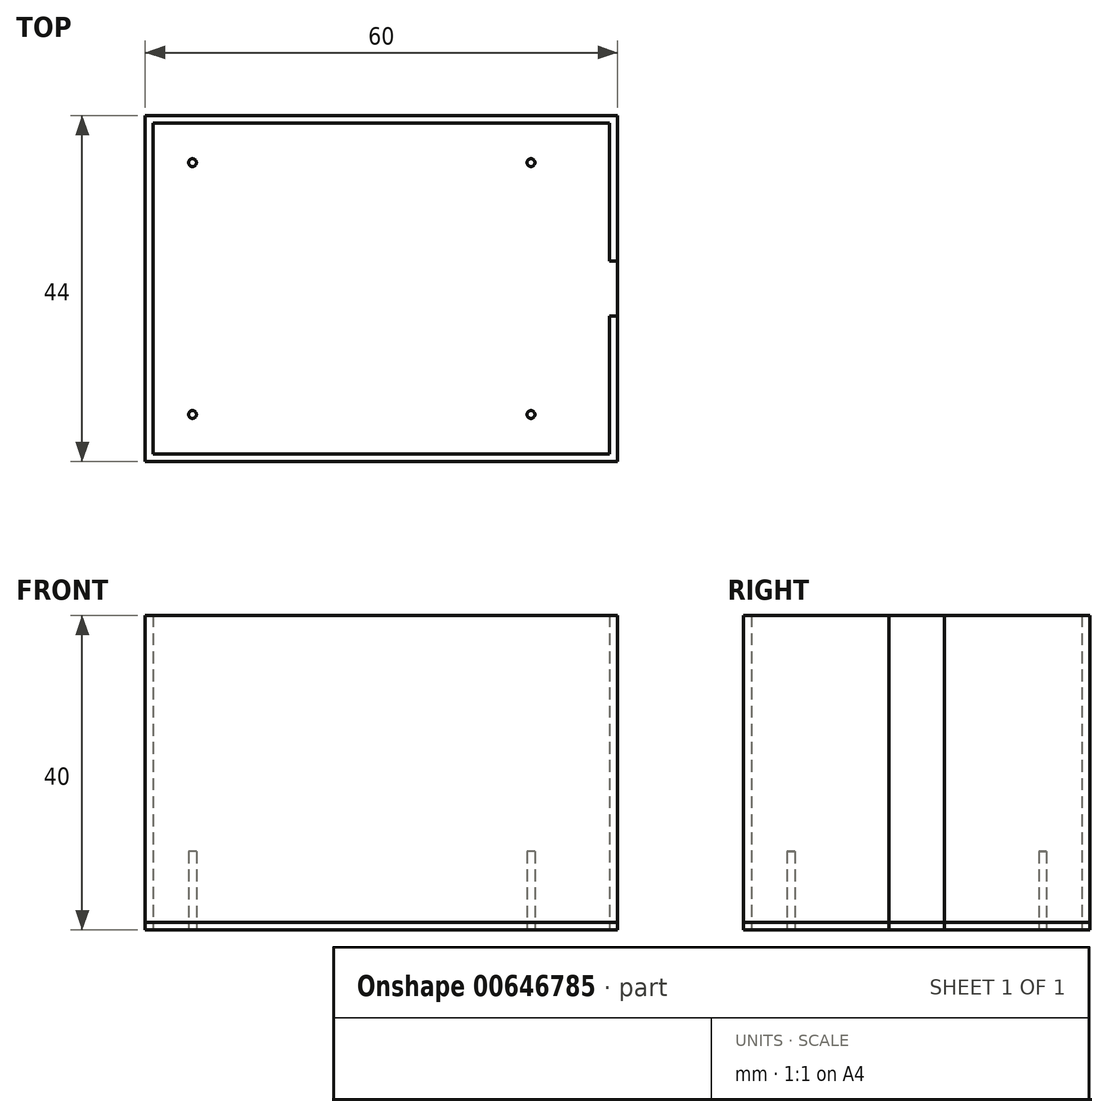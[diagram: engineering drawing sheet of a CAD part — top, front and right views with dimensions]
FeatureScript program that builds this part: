
annotation { "Feature Type Name" : "Feature", "Feature Type Description" : "" }
export const myFeature = defineFeature(function(context is Context, id is Id, definition is map)
    precondition{}
    {
        {
            var Q0;
            Q0=qCreatedBy(makeId("Top.planeOp"),FACE);
            var sketch = newSketch(context, id + "F0", { "sketchPlane" : qUnion([Q0])});
            skLineSegment(sketch, "E0", {"start": v(-43, 0) * mm, "end": v(0, 0) * mm});
            skLineSegment(sketch, "E1", {"start": v(0, 0) * mm, "end": v(0, 32) * mm});
            skLineSegment(sketch, "E2", {"start": v(0, 32) * mm, "end": v(-43, 32) * mm});
            skLineSegment(sketch, "E3", {"start": v(-43, 32) * mm, "end": v(-43, 0) * mm});
            skLineSegment(sketch, "E4.0", {"start": v(-48, -5) * mm, "end": v(10, -5) * mm});
            skLineSegment(sketch, "E4.1", {"start": v(-48, 37) * mm, "end": v(-48, -5) * mm});
            skLineSegment(sketch, "E4.2", {"start": v(10, 37) * mm, "end": v(-48, 37) * mm});
            skLineSegment(sketch, "E5.0", {"start": v(10, -5) * mm, "end": v(10, 37) * mm});
            skCircle(sketch, "E6", {"center": v(-43, 32) * mm, "radius": 0.5 * mm});
            skCircle(sketch, "E7", {"center": v(0, 32) * mm, "radius": 0.5 * mm});
            skCircle(sketch, "E8", {"center": v(-43, 0) * mm, "radius": 0.5 * mm});
            skCircle(sketch, "E9", {"center": v(0, 0) * mm, "radius": 0.5 * mm});
            skLineSegment(sketch, "E10.0", {"start": v(11, 38) * mm, "end": v(-49, 38) * mm});
            skLineSegment(sketch, "E10.1", {"start": v(11, -6) * mm, "end": v(11, 38) * mm});
            skLineSegment(sketch, "E10.2", {"start": v(-49, -6) * mm, "end": v(11, -6) * mm});
            skLineSegment(sketch, "E10.3", {"start": v(-49, 38) * mm, "end": v(-49, -6) * mm});
            skLineSegment(sketch, "E11", {"start": v(10, 19.5) * mm, "end": v(11, 19.5) * mm});
            skLineSegment(sketch, "E12", {"start": v(10, 12.5) * mm, "end": v(11, 12.5) * mm});
            skLineSegment(sketch, "E13", {"start": v(10, 19.5) * mm, "end": v(10, 12.5) * mm});
            skLineSegment(sketch, "E14", {"start": v(11, 12.5) * mm, "end": v(11, 19.5) * mm});
            skPoint(sketch, "E15", {"position": v(10, 16) * mm});
            skSolve(sketch);
        }
        {
            var Q0;
            Q0=makeQuery(id+"F0.imprint","IMPRINT",FACE,{"disambiguationData":[TD([[makeQuery(id+"F0.imprint","IMPRINT",EDGE,{"derivedFrom":sQuery(id+"F0.wireOp",EDGE,"E4.0")}),-1.0]])]});
            extrude(context, id + "F1", {"entities" : qUnion([Q0]), "depth" : 40 * mm, "offsetDistance" : 25 * mm});
        }
        {
            var Q0;
            Q0=makeQuery(id+"F0.imprint","IMPRINT",FACE,{"disambiguationData":[TD([[makeQuery(id+"F0.imprint","IMPRINT",EDGE,{"derivedFrom":sQuery(id+"F0.wireOp",EDGE,"E4.0")}),-1.0]])]});
            var Q1;
            {var subQ3=sQuery(id+"F0.wireOp",EDGE,"E8");var subQ13=sQuery(id+"F0.wireOp",EDGE,"E0");var subQ14=makeQuery(id+"F0.imprint","INTERSECT",VERTEX,{"derivedFrom":[subQ13,subQ3]});Q1=makeQuery(id+"F0.imprint","IMPRINT",FACE,{"disambiguationData":[TD([[makeQuery(id+"F0.imprint","IMPRINT",EDGE,{"disambiguationData":[TD([[subQ14,-1.0]])],"derivedFrom":subQ13}),1.0]])]});}
            var Q2;
            Q2=makeQuery(id+"F0.imprint","IMPRINT",FACE,{"disambiguationData":[TD([[makeQuery(id+"F0.imprint","IMPRINT",EDGE,{"derivedFrom":sQuery(id+"F0.wireOp",EDGE,"E4.0")}),1.0]])]});
            var Q3;
            {var subQ0=sQuery(id+"F0.wireOp",EDGE,"E3");var subQ1=sQuery(id+"F0.wireOp",EDGE,"E0");var subQ2=makeQuery(id+"F0.imprint","INTERSECT",VERTEX,{"derivedFrom":[subQ1,subQ0]});Q3=makeQuery(id+"F0.imprint","IMPRINT",FACE,{"disambiguationData":[TD([[makeQuery(id+"F0.imprint","IMPRINT",EDGE,{"disambiguationData":[TD([[subQ2,-1.0]])],"derivedFrom":subQ1}),-1.0]])]});}
            var Q4;
            {var subQ0=sQuery(id+"F0.wireOp",EDGE,"E3");var subQ1=sQuery(id+"F0.wireOp",EDGE,"E0");var subQ2=makeQuery(id+"F0.imprint","INTERSECT",VERTEX,{"derivedFrom":[subQ1,subQ0]});Q4=makeQuery(id+"F0.imprint","IMPRINT",FACE,{"disambiguationData":[TD([[makeQuery(id+"F0.imprint","IMPRINT",EDGE,{"disambiguationData":[TD([[subQ2,-1.0]])],"derivedFrom":subQ1}),1.0]])]});}
            var Q5;
            {var subQ0=sQuery(id+"F0.wireOp",EDGE,"E1");var subQ1=sQuery(id+"F0.wireOp",EDGE,"E0");var subQ2=makeQuery(id+"F0.imprint","INTERSECT",VERTEX,{"derivedFrom":[subQ1,subQ0]});Q5=makeQuery(id+"F0.imprint","IMPRINT",FACE,{"disambiguationData":[TD([[makeQuery(id+"F0.imprint","IMPRINT",EDGE,{"disambiguationData":[TD([[subQ2,1.0]])],"derivedFrom":subQ1}),1.0]])]});}
            var Q6;
            {var subQ0=sQuery(id+"F0.wireOp",EDGE,"E1");var subQ1=sQuery(id+"F0.wireOp",EDGE,"E0");var subQ2=makeQuery(id+"F0.imprint","INTERSECT",VERTEX,{"derivedFrom":[subQ1,subQ0]});Q6=makeQuery(id+"F0.imprint","IMPRINT",FACE,{"disambiguationData":[TD([[makeQuery(id+"F0.imprint","IMPRINT",EDGE,{"disambiguationData":[TD([[subQ2,1.0]])],"derivedFrom":subQ1}),-1.0]])]});}
            var Q7;
            {var subQ0=sQuery(id+"F0.wireOp",EDGE,"E2");var subQ1=sQuery(id+"F0.wireOp",EDGE,"E1");var subQ2=makeQuery(id+"F0.imprint","INTERSECT",VERTEX,{"derivedFrom":[subQ1,subQ0]});Q7=makeQuery(id+"F0.imprint","IMPRINT",FACE,{"disambiguationData":[TD([[makeQuery(id+"F0.imprint","IMPRINT",EDGE,{"disambiguationData":[TD([[subQ2,1.0]])],"derivedFrom":subQ1}),1.0]])]});}
            var Q8;
            {var subQ0=sQuery(id+"F0.wireOp",EDGE,"E2");var subQ1=sQuery(id+"F0.wireOp",EDGE,"E1");var subQ2=makeQuery(id+"F0.imprint","INTERSECT",VERTEX,{"derivedFrom":[subQ1,subQ0]});Q8=makeQuery(id+"F0.imprint","IMPRINT",FACE,{"disambiguationData":[TD([[makeQuery(id+"F0.imprint","IMPRINT",EDGE,{"disambiguationData":[TD([[subQ2,1.0]])],"derivedFrom":subQ1}),-1.0]])]});}
            var Q9;
            {var subQ0=sQuery(id+"F0.wireOp",EDGE,"E3");var subQ1=sQuery(id+"F0.wireOp",EDGE,"E2");var subQ2=makeQuery(id+"F0.imprint","INTERSECT",VERTEX,{"derivedFrom":[subQ1,subQ0]});Q9=makeQuery(id+"F0.imprint","IMPRINT",FACE,{"disambiguationData":[TD([[makeQuery(id+"F0.imprint","IMPRINT",EDGE,{"disambiguationData":[TD([[subQ2,1.0]])],"derivedFrom":subQ1}),-1.0]])]});}
            var Q10;
            {var subQ0=sQuery(id+"F0.wireOp",EDGE,"E3");var subQ1=sQuery(id+"F0.wireOp",EDGE,"E2");var subQ2=makeQuery(id+"F0.imprint","INTERSECT",VERTEX,{"derivedFrom":[subQ1,subQ0]});Q10=makeQuery(id+"F0.imprint","IMPRINT",FACE,{"disambiguationData":[TD([[makeQuery(id+"F0.imprint","IMPRINT",EDGE,{"disambiguationData":[TD([[subQ2,1.0]])],"derivedFrom":subQ1}),1.0]])]});}
            var Q11;
            Q11 = qSketchRegion(id + "F0", true);
            extrude(context, id + "F2", {"entities" : qUnion([Q0, Q1, Q2, Q3, Q4, Q5, Q6, Q7, Q8, Q9, Q10, Q11]), "depth" : 1 * mm, "offsetDistance" : 25 * mm});
        }
        {
            var Q0;
            {var subQ0=sQuery(id+"F0.wireOp",EDGE,"E3");var subQ1=sQuery(id+"F0.wireOp",EDGE,"E2");var subQ2=makeQuery(id+"F0.imprint","INTERSECT",VERTEX,{"derivedFrom":[subQ1,subQ0]});Q0=makeQuery(id+"F0.imprint","IMPRINT",FACE,{"disambiguationData":[TD([[makeQuery(id+"F0.imprint","IMPRINT",EDGE,{"disambiguationData":[TD([[subQ2,1.0]])],"derivedFrom":subQ1}),-1.0]])]});}
            var Q1;
            {var subQ0=sQuery(id+"F0.wireOp",EDGE,"E3");var subQ1=sQuery(id+"F0.wireOp",EDGE,"E2");var subQ2=makeQuery(id+"F0.imprint","INTERSECT",VERTEX,{"derivedFrom":[subQ1,subQ0]});Q1=makeQuery(id+"F0.imprint","IMPRINT",FACE,{"disambiguationData":[TD([[makeQuery(id+"F0.imprint","IMPRINT",EDGE,{"disambiguationData":[TD([[subQ2,1.0]])],"derivedFrom":subQ1}),1.0]])]});}
            var Q2;
            {var subQ0=sQuery(id+"F0.wireOp",EDGE,"E2");var subQ1=sQuery(id+"F0.wireOp",EDGE,"E1");var subQ2=makeQuery(id+"F0.imprint","INTERSECT",VERTEX,{"derivedFrom":[subQ1,subQ0]});Q2=makeQuery(id+"F0.imprint","IMPRINT",FACE,{"disambiguationData":[TD([[makeQuery(id+"F0.imprint","IMPRINT",EDGE,{"disambiguationData":[TD([[subQ2,1.0]])],"derivedFrom":subQ1}),1.0]])]});}
            var Q3;
            {var subQ0=sQuery(id+"F0.wireOp",EDGE,"E2");var subQ1=sQuery(id+"F0.wireOp",EDGE,"E1");var subQ2=makeQuery(id+"F0.imprint","INTERSECT",VERTEX,{"derivedFrom":[subQ1,subQ0]});Q3=makeQuery(id+"F0.imprint","IMPRINT",FACE,{"disambiguationData":[TD([[makeQuery(id+"F0.imprint","IMPRINT",EDGE,{"disambiguationData":[TD([[subQ2,1.0]])],"derivedFrom":subQ1}),-1.0]])]});}
            var Q4;
            {var subQ0=sQuery(id+"F0.wireOp",EDGE,"E1");var subQ1=sQuery(id+"F0.wireOp",EDGE,"E0");var subQ2=makeQuery(id+"F0.imprint","INTERSECT",VERTEX,{"derivedFrom":[subQ1,subQ0]});Q4=makeQuery(id+"F0.imprint","IMPRINT",FACE,{"disambiguationData":[TD([[makeQuery(id+"F0.imprint","IMPRINT",EDGE,{"disambiguationData":[TD([[subQ2,1.0]])],"derivedFrom":subQ1}),-1.0]])]});}
            var Q5;
            {var subQ0=sQuery(id+"F0.wireOp",EDGE,"E1");var subQ1=sQuery(id+"F0.wireOp",EDGE,"E0");var subQ2=makeQuery(id+"F0.imprint","INTERSECT",VERTEX,{"derivedFrom":[subQ1,subQ0]});Q5=makeQuery(id+"F0.imprint","IMPRINT",FACE,{"disambiguationData":[TD([[makeQuery(id+"F0.imprint","IMPRINT",EDGE,{"disambiguationData":[TD([[subQ2,1.0]])],"derivedFrom":subQ1}),1.0]])]});}
            var Q6;
            {var subQ0=sQuery(id+"F0.wireOp",EDGE,"E3");var subQ1=sQuery(id+"F0.wireOp",EDGE,"E0");var subQ2=makeQuery(id+"F0.imprint","INTERSECT",VERTEX,{"derivedFrom":[subQ1,subQ0]});Q6=makeQuery(id+"F0.imprint","IMPRINT",FACE,{"disambiguationData":[TD([[makeQuery(id+"F0.imprint","IMPRINT",EDGE,{"disambiguationData":[TD([[subQ2,-1.0]])],"derivedFrom":subQ1}),1.0]])]});}
            var Q7;
            {var subQ0=sQuery(id+"F0.wireOp",EDGE,"E3");var subQ1=sQuery(id+"F0.wireOp",EDGE,"E0");var subQ2=makeQuery(id+"F0.imprint","INTERSECT",VERTEX,{"derivedFrom":[subQ1,subQ0]});Q7=makeQuery(id+"F0.imprint","IMPRINT",FACE,{"disambiguationData":[TD([[makeQuery(id+"F0.imprint","IMPRINT",EDGE,{"disambiguationData":[TD([[subQ2,-1.0]])],"derivedFrom":subQ1}),-1.0]])]});}
            extrude(context, id + "F3", {"entities" : qUnion([Q0, Q1, Q2, Q3, Q4, Q5, Q6, Q7]), "depth" : 10 * mm, "offsetDistance" : 25 * mm});
        }
    });
